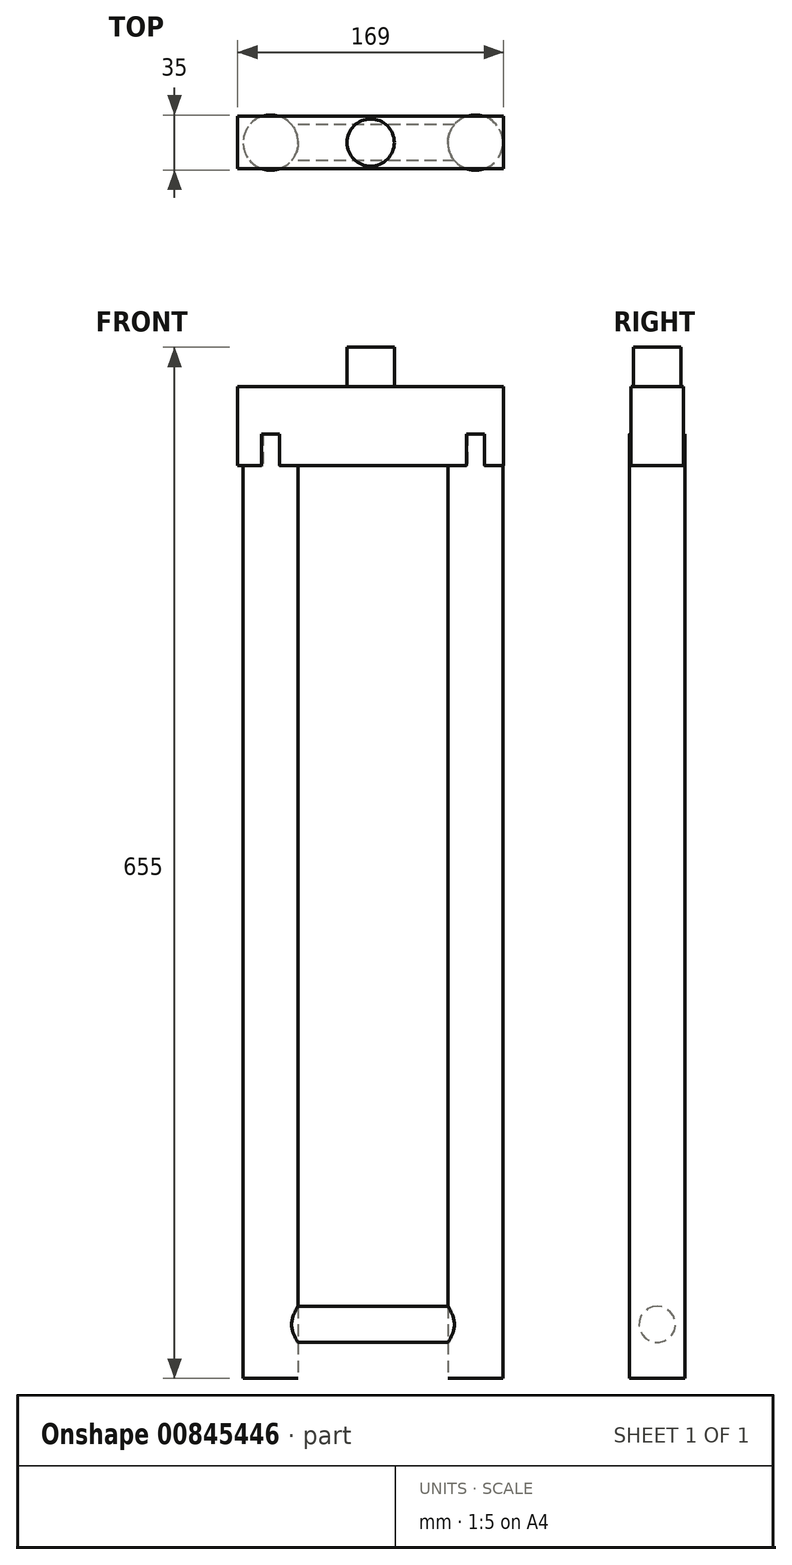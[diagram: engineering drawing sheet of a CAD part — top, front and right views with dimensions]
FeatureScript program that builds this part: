
annotation { "Feature Type Name" : "Feature", "Feature Type Description" : "" }
export const myFeature = defineFeature(function(context is Context, id is Id, definition is map)
    precondition{}
    {
        {
            var Q0;
            Q0=qCreatedBy(makeId("Top.planeOp"),FACE);
            var sketch = newSketch(context, id + "F0", { "sketchPlane" : qUnion([Q0])});
            skCircle(sketch, "E0", {"center": v(-39.4, 0) * mm, "radius": 17.5 * mm});
            skCircle(sketch, "E1", {"center": v(90.6, 0) * mm, "radius": 17.5 * mm});
            skSolve(sketch);
        }
        {
            var Q0;
            Q0 = qSketchRegion(id + "F0", true);
            extrude(context, id + "F1", {"entities" : qUnion([Q0]), "depth" : 600 * mm, "offsetDistance" : 25 * mm});
        }
        {
            var Q0;
            Q0=qCreatedBy(makeId("Right.planeOp"),FACE);
            var sketch = newSketch(context, id + "F2", { "sketchPlane" : qUnion([Q0])});
            skCircle(sketch, "E2", {"center": v(0, 34.3) * mm, "radius": 11.5 * mm});
            skSolve(sketch);
        }
        {
            var Q0;
            Q0 = qSketchRegion(id + "F2", true);
            extrude(context, id + "F3", {"entities" : qUnion([Q0]), "endBound" : BoundingType.UP_TO_NEXT, "depth" : 25 * mm, "offsetDistance" : 25 * mm, "hasSecondDirection" : true, "secondDirectionBound" : BoundingType.UP_TO_NEXT, "secondDirectionOppositeDirection" : true, "secondDirectionDepth" : 25 * mm});
        }
        {
            var Q0;
            Q0=qCreatedBy(makeId("Top.planeOp"),FACE);
            cPlane(context, id + "F4", {"entities" : qUnion([Q0]), "cplaneType" : CPlaneType.OFFSET, "offset" : 630 * mm, "width" : 150 * mm, "height" : 150 * mm});
        }
        {
            var Q0;
            Q0=qCreatedBy(id+"F4.planeOp",FACE);
            var sketch = newSketch(context, id + "F5", { "sketchPlane" : qUnion([Q0])});
            skLineSegment(sketch, "E3.bottom", {"start": v(-60.4, 16.77) * mm, "end": v(108.6, 16.77) * mm});
            skLineSegment(sketch, "E3.top", {"start": v(-60.4, -16.55) * mm, "end": v(108.6, -16.55) * mm});
            skLineSegment(sketch, "E3.left", {"start": v(-60.4, 16.77) * mm, "end": v(-60.4, -16.55) * mm});
            skLineSegment(sketch, "E3.right", {"start": v(108.6, 16.77) * mm, "end": v(108.6, -16.55) * mm});
            skSolve(sketch);
        }
        {
            var Q0;
            Q0=makeQuery(id+"F5.imprint","IMPRINT",FACE,{"disambiguationData":[TD([[makeQuery(id+"F5.imprint","IMPRINT",EDGE,{"derivedFrom":sQuery(id+"F5.wireOp",EDGE,"E3.bottom")}),-1.0]])]});
            extrude(context, id + "F6", {"entities" : qUnion([Q0]), "operationType" : NewBodyOperationType.ADD, "oppositeDirection" : true, "depth" : 50 * mm, "offsetDistance" : 25 * mm});
        }
        {
            var Q0;
            Q0=makeQuery(id+"F6.opExtrude","CAP_FACE",FACE,{"disambiguationData":[OSD([sQuery(id+"F5.wireOp",EDGE,"E3.bottom"),sQuery(id+"F5.wireOp",EDGE,"E3.top"),sQuery(id+"F5.wireOp",EDGE,"E3.left"),sQuery(id+"F5.wireOp",EDGE,"E3.right")])],"isStart":true});
            var sketch = newSketch(context, id + "F7", { "sketchPlane" : qUnion([Q0])});
            skCircle(sketch, "E4", {"center": v(24.1, 0) * mm, "radius": 15 * mm});
            skSolve(sketch);
        }
        {
            var Q0;
            Q0=makeQuery(id+"F7.imprint","IMPRINT",FACE,{"disambiguationData":[TD([[makeQuery(id+"F7.imprint","IMPRINT",EDGE,{"derivedFrom":sQuery(id+"F7.wireOp",EDGE,"E4")}),1.0]])]});
            extrude(context, id + "F8", {"entities" : qUnion([Q0]), "operationType" : NewBodyOperationType.ADD, "depth" : 25 * mm, "offsetDistance" : 25 * mm});
        }
    });
